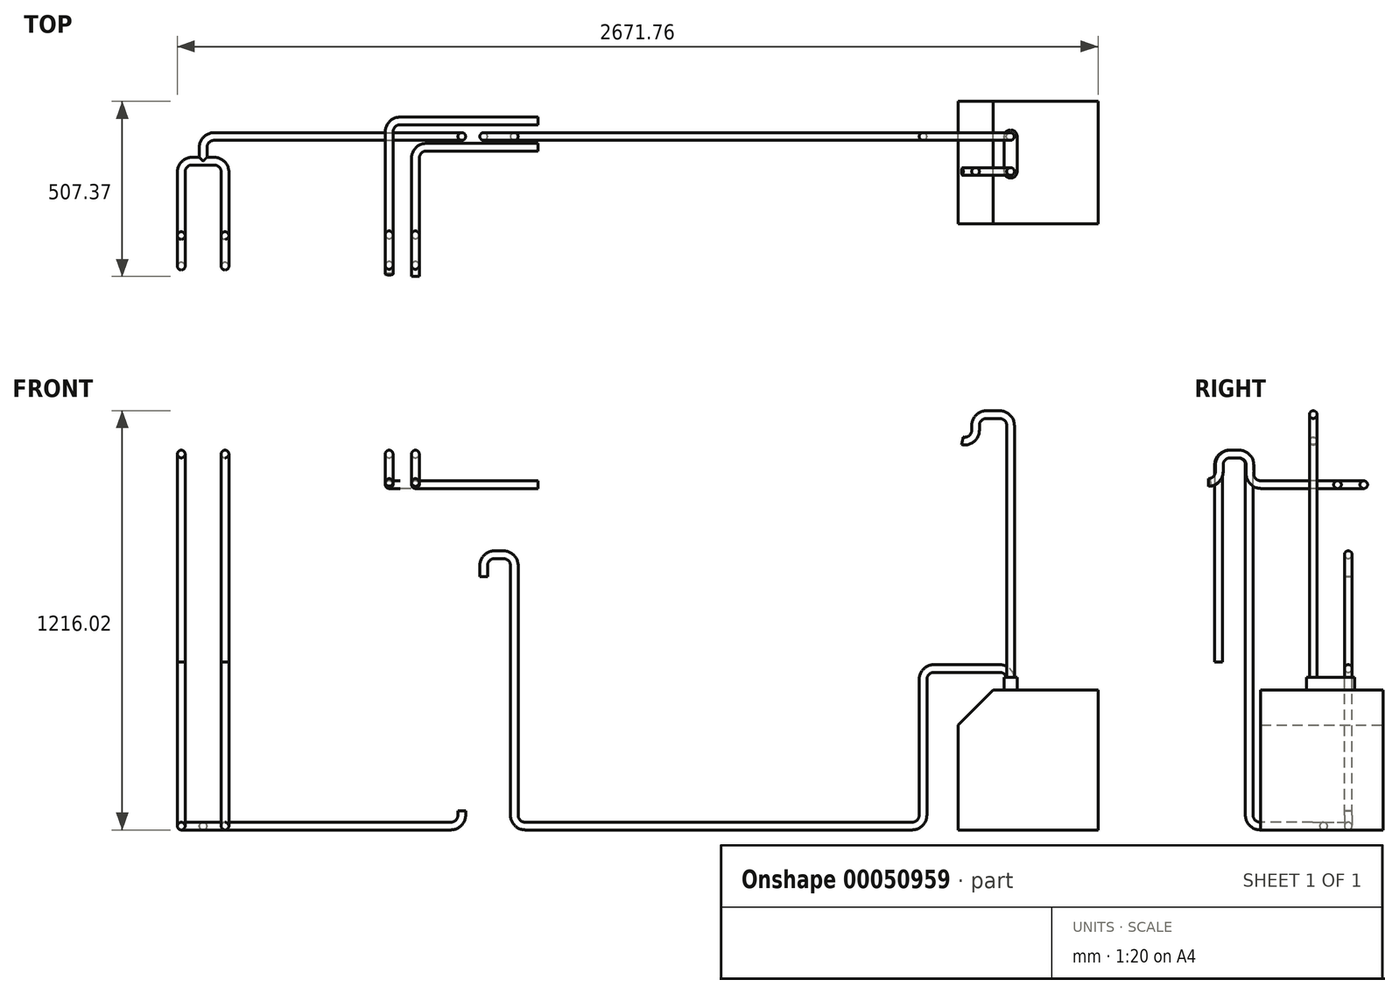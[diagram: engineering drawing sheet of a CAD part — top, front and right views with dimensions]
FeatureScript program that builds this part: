
annotation { "Feature Type Name" : "Feature", "Feature Type Description" : "" }
export const myFeature = defineFeature(function(context is Context, id is Id, definition is map)
    precondition{}
    {
        {
            var Q0;
            Q0=qCreatedBy(makeId("Right.planeOp"),FACE);
            var sketch = newSketch(context, id + "F0", { "sketchPlane" : qUnion([Q0])});
            skLineSegment(sketch, "E0", {"start": v(-273.05, 476.25) * mm, "end": v(-273.05, 1047.75) * mm});
            skLineSegment(sketch, "E1", {"start": v(-241.3, 1079.5) * mm, "end": v(-215.9, 1079.5) * mm});
            skLineSegment(sketch, "E2", {"start": v(-184.15, 1047.75) * mm, "end": v(-184.15, 31.75) * mm});
            skLineSegment(sketch, "E3", {"start": v(-152.4, 0) * mm, "end": v(0, 0) * mm});
            skPoint(sketch, "E4.visualSharp", {"position": v(-273.05, 1079.5) * mm});
            skArc(sketch, "E4.filletArc", {"start": v(-241.3, 1079.5) * mm, "mid": v(-263.75, 1070.2) * mm, "end": v(-273.05, 1047.75) * mm});
            skPoint(sketch, "E5.visualSharp", {"position": v(-184.15, 1079.5) * mm});
            skArc(sketch, "E5.filletArc", {"start": v(-184.15, 1047.75) * mm, "mid": v(-193.45, 1070.2) * mm, "end": v(-215.9, 1079.5) * mm});
            skPoint(sketch, "E6.visualSharp", {"position": v(-184.15, 0) * mm});
            skArc(sketch, "E6.filletArc", {"start": v(-184.15, 31.75) * mm, "mid": v(-174.85, 9.3) * mm, "end": v(-152.4, 0) * mm});
            skSolve(sketch);
        }
        {
            var Q0;
            Q0=qCreatedBy(makeId("Top.planeOp"),FACE);
            var sketch = newSketch(context, id + "F1", { "sketchPlane" : qUnion([Q0])});
            skLineSegment(sketch, "E7", {"start": v(31.75, 31.75) * mm, "end": v(95.25, 31.75) * mm});
            skPoint(sketch, "E8.visualSharp", {"position": v(-6.35, 31.75) * mm});
            skArc(sketch, "E8.filletArc", {"start": v(31.75, 31.75) * mm, "mid": v(9.3, 22.45) * mm, "end": v(0, 0) * mm});
            skPoint(sketch, "E9.visualSharp", {"position": v(280.99, 31.75) * mm});
            skArc(sketch, "E9.filletArc", {"start": v(127, 0) * mm, "mid": v(117.7, 22.45) * mm, "end": v(95.25, 31.75) * mm});
            skPoint(sketch, "E10.visualSharp", {"position": v(82.55, 82.55) * mm});
            skSolve(sketch);
        }
        {
            var Q0;
            Q0=qCreatedBy(makeId("Front.planeOp"),FACE);
            var sketch = newSketch(context, id + "F2", { "sketchPlane" : qUnion([Q0])});
            skCircle(sketch, "E11", {"center": v(0, 0) * mm, "radius": 11.11 * mm});
            skSolve(sketch);
        }
        {
            var Q0;
            Q0=qCreatedBy(makeId("Right.planeOp"),FACE);
            var Q1;
            Q1=sQuery(id+"F1.wireOp",VERTEX,"E9.filletArc.start");
            cPlane(context, id + "F3", {"entities" : qUnion([Q0, Q1]), "cplaneType" : CPlaneType.PLANE_POINT, "offset" : 25.4 * mm, "width" : 152.4 * mm, "height" : 152.4 * mm});
        }
        {
            var Q0;
            Q0=qCreatedBy(id+"F3.planeOp",FACE);
            var sketch = newSketch(context, id + "F4", { "sketchPlane" : qUnion([Q0])});
            skLineSegment(sketch, "E12", {"start": v(0, 0) * mm, "end": v(-152.4, 0) * mm});
            skLineSegment(sketch, "E13", {"start": v(-184.15, 31.75) * mm, "end": v(-184.15, 1047.75) * mm});
            skLineSegment(sketch, "E14", {"start": v(-215.9, 1079.5) * mm, "end": v(-241.3, 1079.5) * mm});
            skLineSegment(sketch, "E15", {"start": v(-273.05, 1047.75) * mm, "end": v(-273.05, 476.25) * mm});
            skPoint(sketch, "E16.visualSharp", {"position": v(-273.05, 1079.5) * mm});
            skArc(sketch, "E16.filletArc", {"start": v(-241.3, 1079.5) * mm, "mid": v(-263.75, 1070.2) * mm, "end": v(-273.05, 1047.75) * mm});
            skPoint(sketch, "E17.visualSharp", {"position": v(-184.15, 1079.5) * mm});
            skArc(sketch, "E17.filletArc", {"start": v(-184.15, 1047.75) * mm, "mid": v(-193.45, 1070.2) * mm, "end": v(-215.9, 1079.5) * mm});
            skPoint(sketch, "E18.visualSharp", {"position": v(-184.15, 0) * mm});
            skArc(sketch, "E18.filletArc", {"start": v(-184.15, 31.75) * mm, "mid": v(-174.85, 9.3) * mm, "end": v(-152.4, 0) * mm});
            skSolve(sketch);
        }
        {
            var Q0;
            Q0=makeQuery(id+"F2.imprint","IMPRINT",FACE,{"disambiguationData":[TD([[makeQuery(id+"F2.imprint","IMPRINT",EDGE,{"derivedFrom":sQuery(id+"F2.wireOp",EDGE,"E11")}),1.0]])]});
            var Q1;
            Q1 = qConstructionFilter(qBodyType(qCreatedBy(id + "F0" ,EDGE), BodyType.WIRE), ConstructionObject.NO);
            sweep(context, id + "F5", {"profiles" : qUnion([Q0]), "path" : qUnion([Q1])});
        }
        {
            var Q0;
            Q0=makeQuery(id+"F2.imprint","IMPRINT",FACE,{"disambiguationData":[TD([[makeQuery(id+"F2.imprint","IMPRINT",EDGE,{"derivedFrom":sQuery(id+"F2.wireOp",EDGE,"E11")}),1.0]])]});
            var Q1;
            Q1=sQuery(id+"F1.wireOp",EDGE,"E8.filletArc");
            var Q2;
            Q2=sQuery(id+"F1.wireOp",EDGE,"E7");
            var Q3;
            Q3=sQuery(id+"F1.wireOp",EDGE,"E9.filletArc");
            var Q4;
            Q4=sQuery(id+"F4.wireOp",EDGE,"E12");
            var Q5;
            Q5=sQuery(id+"F4.wireOp",EDGE,"E18.filletArc");
            var Q6;
            Q6=sQuery(id+"F4.wireOp",EDGE,"E13");
            var Q7;
            Q7=sQuery(id+"F4.wireOp",EDGE,"E17.filletArc");
            var Q8;
            Q8=sQuery(id+"F4.wireOp",EDGE,"E14");
            var Q9;
            Q9=sQuery(id+"F4.wireOp",EDGE,"E16.filletArc");
            var Q10;
            Q10=sQuery(id+"F4.wireOp",EDGE,"E15");
            sweep(context, id + "F6", {"operationType" : NewBodyOperationType.ADD, "profiles" : qUnion([Q0]), "path" : qUnion([Q1, Q2, Q3, Q4, Q5, Q6, Q7, Q8, Q9, Q10])});
        }
        {
            var Q0;
            Q0=qCreatedBy(makeId("Top.planeOp"),FACE);
            var sketch = newSketch(context, id + "F7", { "sketchPlane" : qUnion([Q0])});
            skLineSegment(sketch, "E19", {"start": v(63.5, 31.75) * mm, "end": v(63.5, 71.48) * mm});
            skLineSegment(sketch, "E20", {"start": v(95.25, 103.23) * mm, "end": v(782.32, 103.23) * mm});
            skPoint(sketch, "E21.visualSharp", {"position": v(63.5, 103.23) * mm});
            skArc(sketch, "E21.filletArc", {"start": v(95.25, 103.23) * mm, "mid": v(72.8, 93.93) * mm, "end": v(63.5, 71.48) * mm});
            skLineSegment(sketch, "E22.trimOffspring", {"start": v(998.22, 103.23) * mm, "end": v(2120.9, 103.23) * mm});
            skSolve(sketch);
        }
        {
            var Q0;
            Q0=qCreatedBy(makeId("Right.planeOp"),FACE);
            var Q1;
            Q1=sQuery(id+"F7.wireOp",VERTEX,"E22.trimOffspring.start");
            cPlane(context, id + "F8", {"entities" : qUnion([Q0, Q1]), "cplaneType" : CPlaneType.PLANE_POINT, "offset" : 25.4 * mm, "width" : 152.4 * mm, "height" : 152.4 * mm});
        }
        {
            var Q0;
            Q0=qCreatedBy(id+"F8.planeOp",FACE);
            var sketch = newSketch(context, id + "F9", { "sketchPlane" : qUnion([Q0])});
            skCircle(sketch, "E23", {"center": v(103.23, 0) * mm, "radius": 11.11 * mm});
            skSolve(sketch);
        }
        {
            var Q0;
            Q0=makeQuery(id+"F9.imprint","IMPRINT",FACE,{"disambiguationData":[TD([[makeQuery(id+"F9.imprint","IMPRINT",EDGE,{"derivedFrom":sQuery(id+"F9.wireOp",EDGE,"E23")}),1.0]])]});
            var Q1;
            Q1=sQuery(id+"F7.wireOp",EDGE,"E22.trimOffspring");
            sweep(context, id + "F10", {"profiles" : qUnion([Q0]), "path" : qUnion([Q1])});
        }
        {
            var Q0;
            Q0=sQuery(id+"F1.wireOp",EDGE,"E7");
            cPoint(context, id + "F11", {"entities" : qUnion([Q0]), "parameter" : 0.5});
        }
        {
            var Q0;
            Q0=qCreatedBy(makeId("Front.planeOp"),FACE);
            var Q1;
            Q1 = qCreatedBy(id + "F11" ,VERTEX);
            cPlane(context, id + "F12", {"entities" : qUnion([Q0, Q1]), "cplaneType" : CPlaneType.PLANE_POINT, "offset" : 25.4 * mm, "width" : 152.4 * mm, "height" : 152.4 * mm});
        }
        {
            var Q0;
            Q0=qCreatedBy(id+"F12.planeOp",FACE);
            var sketch = newSketch(context, id + "F13", { "sketchPlane" : qUnion([Q0])});
            skCircle(sketch, "E24", {"center": v(63.5, 0) * mm, "radius": 11.11 * mm});
            skSolve(sketch);
        }
        {
            var Q0;
            Q0=qCreatedBy(makeId("Front.planeOp"),FACE);
            var Q1;
            Q1=sQuery(id+"F7.wireOp",VERTEX,"E20.end");
            cPlane(context, id + "F14", {"entities" : qUnion([Q0, Q1]), "cplaneType" : CPlaneType.PLANE_POINT, "offset" : 25.4 * mm, "width" : 152.4 * mm, "height" : 152.4 * mm});
        }
        {
            var Q0;
            Q0 = qSketchRegion(id + "F13", true);
            var Q1;
            Q1=sQuery(id+"F7.wireOp",EDGE,"E19");
            var Q2;
            Q2=sQuery(id+"F7.wireOp",EDGE,"E21.filletArc");
            var Q3;
            Q3=sQuery(id+"F7.wireOp",EDGE,"E20");
            sweep(context, id + "F15", {"operationType" : NewBodyOperationType.ADD, "profiles" : qUnion([Q0]), "path" : qUnion([Q1, Q2, Q3])});
        }
        {
            var Q0;
            Q0=qCreatedBy(id+"F14.planeOp",FACE);
            var sketch = newSketch(context, id + "F16", { "sketchPlane" : qUnion([Q0])});
            skLineSegment(sketch, "E25", {"start": v(2152.65, 31.75) * mm, "end": v(2152.65, 425.45) * mm});
            skLineSegment(sketch, "E26", {"start": v(2184.4, 457.2) * mm, "end": v(2374.9, 457.2) * mm});
            skLineSegment(sketch, "E27", {"start": v(2406.65, 425.45) * mm, "end": v(2406.65, 395.29) * mm});
            skPoint(sketch, "E28.visualSharp", {"position": v(2152.65, 0) * mm});
            skArc(sketch, "E28.filletArc", {"start": v(2120.9, 0) * mm, "mid": v(2143.35, 9.3) * mm, "end": v(2152.65, 31.75) * mm});
            skPoint(sketch, "E29.visualSharp", {"position": v(2152.65, 457.2) * mm});
            skArc(sketch, "E29.filletArc", {"start": v(2184.4, 457.2) * mm, "mid": v(2161.95, 447.9) * mm, "end": v(2152.65, 425.45) * mm});
            skPoint(sketch, "E30.visualSharp", {"position": v(2406.65, 457.2) * mm});
            skArc(sketch, "E30.filletArc", {"start": v(2406.65, 425.45) * mm, "mid": v(2397.35, 447.9) * mm, "end": v(2374.9, 457.2) * mm});
            skLineSegment(sketch, "E31.bottom", {"start": v(2355.85, 395.29) * mm, "end": v(2660.65, 395.29) * mm});
            skLineSegment(sketch, "E31.top", {"start": v(2254.25, -11.11) * mm, "end": v(2660.65, -11.11) * mm});
            skLineSegment(sketch, "E31.left", {"start": v(2254.25, 293.69) * mm, "end": v(2254.25, -11.11) * mm});
            skLineSegment(sketch, "E31.right", {"start": v(2660.65, 395.29) * mm, "end": v(2660.65, -11.11) * mm});
            skLineSegment(sketch, "E32", {"start": v(2254.25, 293.69) * mm, "end": v(2355.85, 395.29) * mm});
            skSolve(sketch);
        }
        {
            var Q0;
            Q0 = qSketchRegion(id + "F16", true);
            extrude(context, id + "F17", {"entities" : qUnion([Q0]), "depth" : 254 * mm, "hasSecondDirection" : true, "secondDirectionOppositeDirection" : true, "secondDirectionDepth" : 101.6 * mm});
        }
        {
            var Q0;
            Q0=makeQuery(id+"F10.opSweep","CAP_FACE",FACE,{"disambiguationData":[OSD([sQuery(id+"F7.wireOp",VERTEX,"E22.trimOffspring.end"),sQuery(id+"F9.wireOp",EDGE,"E23")])],"isStart":false});
            var Q1;
            Q1=sQuery(id+"F16.wireOp",EDGE,"Az77wKnU-HWYb-h9Rr-81SB-TqBPY5BJPOyP");
            var Q2;
            Q2=sQuery(id+"F16.wireOp",EDGE,"E28.filletArc");
            var Q3;
            Q3=sQuery(id+"F16.wireOp",EDGE,"E25");
            var Q4;
            Q4=sQuery(id+"F16.wireOp",EDGE,"E29.filletArc");
            var Q5;
            Q5=sQuery(id+"F16.wireOp",EDGE,"E26");
            var Q6;
            Q6=sQuery(id+"F16.wireOp",EDGE,"E30.filletArc");
            var Q7;
            Q7=sQuery(id+"F16.wireOp",EDGE,"E27");
            sweep(context, id + "F18", {"operationType" : NewBodyOperationType.ADD, "profiles" : qUnion([Q0]), "path" : qUnion([Q1, Q2, Q3, Q4, Q5, Q6, Q7])});
        }
        {
            var Q0;
            Q0=qCreatedBy(id+"F14.planeOp",FACE);
            cPlane(context, id + "F19", {"entities" : qUnion([Q0]), "cplaneType" : CPlaneType.OFFSET, "offset" : 101.6 * mm, "width" : 152.4 * mm, "height" : 152.4 * mm});
        }
        {
            var Q0;
            Q0=qCreatedBy(id+"F19.planeOp",FACE);
            var sketch = newSketch(context, id + "F20", { "sketchPlane" : qUnion([Q0])});
            skLineSegment(sketch, "E33", {"start": v(2406.65, 381) * mm, "end": v(2406.65, 1162.05) * mm});
            skLineSegment(sketch, "E34", {"start": v(2305.05, 1162.05) * mm, "end": v(2305.05, 1148.7) * mm});
            skLineSegment(sketch, "E35", {"start": v(2336.8, 1193.8) * mm, "end": v(2374.9, 1193.8) * mm});
            skPoint(sketch, "E36.visualSharp", {"position": v(2406.65, 1193.8) * mm});
            skArc(sketch, "E36.filletArc", {"start": v(2406.65, 1162.05) * mm, "mid": v(2397.35, 1184.5) * mm, "end": v(2374.9, 1193.8) * mm});
            skPoint(sketch, "E37.visualSharp", {"position": v(2305.05, 1193.8) * mm});
            skArc(sketch, "E37.filletArc", {"start": v(2336.8, 1193.8) * mm, "mid": v(2314.35, 1184.5) * mm, "end": v(2305.05, 1162.05) * mm});
            skPoint(sketch, "E38.visualSharp", {"position": v(2305.05, 1092.2) * mm});
            skArc(sketch, "E38.filletArc", {"start": v(2266.95, 1117.6) * mm, "mid": v(2293.38, 1124.12) * mm, "end": v(2305.05, 1148.7) * mm});
            skSolve(sketch);
        }
        {
            var Q0;
            Q0=qCreatedBy(makeId("Top.planeOp"),FACE);
            var Q1;
            Q1=sQuery(id+"F20.wireOp",VERTEX,"E33.start");
            cPlane(context, id + "F21", {"entities" : qUnion([Q0, Q1]), "cplaneType" : CPlaneType.PLANE_POINT, "offset" : 25.4 * mm, "width" : 152.4 * mm, "height" : 152.4 * mm});
        }
        {
            var Q0;
            Q0=qCreatedBy(id+"F21.planeOp",FACE);
            var sketch = newSketch(context, id + "F22", { "sketchPlane" : qUnion([Q0])});
            skCircle(sketch, "E39", {"center": v(2406.65, 1.63) * mm, "radius": 11.11 * mm});
            skArc(sketch, "E40", {"start": v(2387.6, 1.63) * mm, "mid": v(2406.65, -17.42) * mm, "end": v(2425.7, 1.63) * mm});
            skLineSegment(sketch, "E41", {"start": v(2387.6, 1.63) * mm, "end": v(2387.6, 103.23) * mm});
            skLineSegment(sketch, "E42", {"start": v(2425.7, 1.63) * mm, "end": v(2425.7, 103.23) * mm});
            skArc(sketch, "E43", {"start": v(2425.7, 103.23) * mm, "mid": v(2406.65, 122.28) * mm, "end": v(2387.6, 103.23) * mm});
            skSolve(sketch);
        }
        {
            var Q0;
            Q0=makeQuery(id+"F22.imprint","IMPRINT",FACE,{"disambiguationData":[TD([[makeQuery(id+"F22.imprint","IMPRINT",EDGE,{"derivedFrom":sQuery(id+"F22.wireOp",EDGE,"E39")}),1.0]])]});
            var Q1;
            Q1=sQuery(id+"F20.wireOp",EDGE,"E33");
            var Q2;
            Q2=sQuery(id+"F20.wireOp",EDGE,"E36.filletArc");
            var Q3;
            Q3=sQuery(id+"F20.wireOp",EDGE,"E35");
            var Q4;
            Q4=sQuery(id+"F20.wireOp",EDGE,"E37.filletArc");
            var Q5;
            Q5=sQuery(id+"F20.wireOp",EDGE,"E34");
            var Q6;
            Q6=sQuery(id+"F20.wireOp",EDGE,"E38.filletArc");
            sweep(context, id + "F23", {"profiles" : qUnion([Q0]), "path" : qUnion([Q1, Q2, Q3, Q4, Q5, Q6])});
        }
        {
            var Q0;
            Q0 = qSketchRegion(id + "F22", true);
            extrude(context, id + "F24", {"entities" : qUnion([Q0]), "operationType" : NewBodyOperationType.ADD, "depth" : 50.8 * mm});
        }
        {
            var Q0;
            Q0=qCreatedBy(makeId("Top.planeOp"),FACE);
            cPlane(context, id + "F25", {"entities" : qUnion([Q0]), "cplaneType" : CPlaneType.OFFSET, "offset" : 990.6 * mm, "width" : 152.4 * mm, "height" : 152.4 * mm});
        }
        {
            var Q0;
            Q0=qCreatedBy(id+"F25.planeOp",FACE);
            var sketch = newSketch(context, id + "F26", { "sketchPlane" : qUnion([Q0])});
            skLineSegment(sketch, "E44", {"start": v(603.25, 116.56) * mm, "end": v(603.25, -150.14) * mm});
            skLineSegment(sketch, "E45", {"start": v(635, 148.31) * mm, "end": v(1035.05, 148.31) * mm});
            skPoint(sketch, "E46.visualSharp", {"position": v(603.25, 148.31) * mm});
            skArc(sketch, "E46.filletArc", {"start": v(635, 148.31) * mm, "mid": v(612.55, 139.01) * mm, "end": v(603.25, 116.56) * mm});
            skLineSegment(sketch, "E47", {"start": v(1035.05, 72.11) * mm, "end": v(711.2, 72.11) * mm});
            skLineSegment(sketch, "E48", {"start": v(679.45, 40.36) * mm, "end": v(679.45, -150.14) * mm});
            skPoint(sketch, "E49.visualSharp", {"position": v(679.45, 72.11) * mm});
            skArc(sketch, "E49.filletArc", {"start": v(711.2, 72.11) * mm, "mid": v(688.75, 62.81) * mm, "end": v(679.45, 40.36) * mm});
            skSolve(sketch);
        }
        {
            var Q0;
            Q0=qCreatedBy(makeId("Right.planeOp"),FACE);
            var Q1;
            Q1=sQuery(id+"F26.wireOp",VERTEX,"E45.end");
            cPlane(context, id + "F27", {"entities" : qUnion([Q0, Q1]), "cplaneType" : CPlaneType.PLANE_POINT, "offset" : 25.4 * mm, "width" : 152.4 * mm, "height" : 152.4 * mm});
        }
        {
            var Q0;
            Q0=qCreatedBy(id+"F27.planeOp",FACE);
            var sketch = newSketch(context, id + "F28", { "sketchPlane" : qUnion([Q0])});
            skCircle(sketch, "E50", {"center": v(148.31, 990.6) * mm, "radius": 11.11 * mm});
            skCircle(sketch, "E51", {"center": v(72.11, 990.6) * mm, "radius": 11.11 * mm});
            skSolve(sketch);
        }
        {
            var Q0;
            Q0=qCreatedBy(id+"F27.planeOp",FACE);
            var Q1;
            Q1=sQuery(id+"F26.wireOp",VERTEX,"E44.end");
            cPlane(context, id + "F29", {"entities" : qUnion([Q0, Q1]), "cplaneType" : CPlaneType.PLANE_POINT, "offset" : 25.4 * mm, "width" : 152.4 * mm, "height" : 152.4 * mm});
        }
        {
            var Q0;
            Q0=qCreatedBy(id+"F29.planeOp",FACE);
            var sketch = newSketch(context, id + "F30", { "sketchPlane" : qUnion([Q0])});
            skLineSegment(sketch, "E52", {"start": v(-181.89, 1022.35) * mm, "end": v(-181.89, 1047.75) * mm});
            skLineSegment(sketch, "E53", {"start": v(-213.64, 1079.5) * mm, "end": v(-239.04, 1079.5) * mm});
            skLineSegment(sketch, "E54", {"start": v(-270.79, 1047.75) * mm, "end": v(-270.79, 1028.06) * mm});
            skPoint(sketch, "E55.visualSharp", {"position": v(-270.79, 1123.55) * mm});
            skArc(sketch, "E55.filletArc", {"start": v(-296.19, 996.95) * mm, "mid": v(-277.94, 1007.98) * mm, "end": v(-270.79, 1028.06) * mm});
            skPoint(sketch, "E56.visualSharp", {"position": v(-270.79, 1079.5) * mm});
            skArc(sketch, "E56.filletArc", {"start": v(-239.04, 1079.5) * mm, "mid": v(-261.49, 1070.2) * mm, "end": v(-270.79, 1047.75) * mm});
            skPoint(sketch, "E57.visualSharp", {"position": v(-181.89, 1079.5) * mm});
            skArc(sketch, "E57.filletArc", {"start": v(-181.89, 1047.75) * mm, "mid": v(-191.19, 1070.2) * mm, "end": v(-213.64, 1079.5) * mm});
            skPoint(sketch, "E58.visualSharp", {"position": v(-181.89, 1009.84) * mm});
            skArc(sketch, "E58.filletArc", {"start": v(-181.89, 1022.35) * mm, "mid": v(-172.59, 999.9) * mm, "end": v(-150.14, 990.6) * mm});
            skSolve(sketch);
        }
        {
            var Q0;
            Q0=makeQuery(id+"F28.imprint","IMPRINT",FACE,{"disambiguationData":[TD([[makeQuery(id+"F28.imprint","IMPRINT",EDGE,{"derivedFrom":sQuery(id+"F28.wireOp",EDGE,"E50")}),1.0]])]});
            var Q1;
            Q1=sQuery(id+"F26.wireOp",EDGE,"E45");
            var Q2;
            Q2=sQuery(id+"F26.wireOp",EDGE,"E46.filletArc");
            var Q3;
            Q3=sQuery(id+"F26.wireOp",EDGE,"E44");
            var Q4;
            Q4=sQuery(id+"F30.wireOp",EDGE,"E58.filletArc");
            var Q5;
            Q5=sQuery(id+"F30.wireOp",EDGE,"E52");
            var Q6;
            Q6=sQuery(id+"F30.wireOp",EDGE,"E57.filletArc");
            var Q7;
            Q7=sQuery(id+"F30.wireOp",EDGE,"E53");
            var Q8;
            Q8=sQuery(id+"F30.wireOp",EDGE,"E56.filletArc");
            var Q9;
            Q9=sQuery(id+"F30.wireOp",EDGE,"E54");
            var Q10;
            Q10=sQuery(id+"F30.wireOp",EDGE,"E55.filletArc");
            sweep(context, id + "F31", {"profiles" : qUnion([Q0]), "path" : qUnion([Q1, Q2, Q3, Q4, Q5, Q6, Q7, Q8, Q9, Q10])});
        }
        {
            var Q0;
            Q0=qCreatedBy(id+"F29.planeOp",FACE);
            var Q1;
            Q1=sQuery(id+"F26.wireOp",VERTEX,"E48.end");
            cPlane(context, id + "F32", {"entities" : qUnion([Q0, Q1]), "cplaneType" : CPlaneType.PLANE_POINT, "offset" : 25.4 * mm, "width" : 152.4 * mm, "height" : 152.4 * mm});
        }
        {
            var Q0;
            Q0=qCreatedBy(id+"F32.planeOp",FACE);
            var sketch = newSketch(context, id + "F33", { "sketchPlane" : qUnion([Q0])});
            skLineSegment(sketch, "E59", {"start": v(-181.89, 1022.35) * mm, "end": v(-181.89, 1047.75) * mm});
            skLineSegment(sketch, "E60", {"start": v(-213.64, 1079.5) * mm, "end": v(-239.04, 1079.5) * mm});
            skLineSegment(sketch, "E61", {"start": v(-270.79, 1047.75) * mm, "end": v(-270.79, 1028.7) * mm});
            skPoint(sketch, "E62.visualSharp", {"position": v(-270.79, 1021) * mm});
            skArc(sketch, "E62.filletArc", {"start": v(-302.54, 996.95) * mm, "mid": v(-280.09, 1006.25) * mm, "end": v(-270.79, 1028.7) * mm});
            skPoint(sketch, "E63.visualSharp", {"position": v(-270.79, 1079.5) * mm});
            skArc(sketch, "E63.filletArc", {"start": v(-239.04, 1079.5) * mm, "mid": v(-261.49, 1070.2) * mm, "end": v(-270.79, 1047.75) * mm});
            skPoint(sketch, "E64.visualSharp", {"position": v(-181.89, 1079.5) * mm});
            skArc(sketch, "E64.filletArc", {"start": v(-181.89, 1047.75) * mm, "mid": v(-191.19, 1070.2) * mm, "end": v(-213.64, 1079.5) * mm});
            skPoint(sketch, "E65.visualSharp", {"position": v(-181.89, 992.4) * mm});
            skArc(sketch, "E65.filletArc", {"start": v(-181.89, 1022.35) * mm, "mid": v(-172.59, 999.9) * mm, "end": v(-150.14, 990.6) * mm});
            skSolve(sketch);
        }
        {
            var Q0;
            Q0=makeQuery(id+"F28.imprint","IMPRINT",FACE,{"disambiguationData":[TD([[makeQuery(id+"F28.imprint","IMPRINT",EDGE,{"derivedFrom":sQuery(id+"F28.wireOp",EDGE,"E51")}),1.0]])]});
            var Q1;
            Q1=sQuery(id+"F26.wireOp",EDGE,"E47");
            var Q2;
            Q2=sQuery(id+"F26.wireOp",EDGE,"E49.filletArc");
            var Q3;
            Q3=sQuery(id+"F26.wireOp",EDGE,"E48");
            var Q4;
            Q4=sQuery(id+"F33.wireOp",EDGE,"E65.filletArc");
            var Q5;
            Q5=sQuery(id+"F33.wireOp",EDGE,"E59");
            var Q6;
            Q6=sQuery(id+"F33.wireOp",EDGE,"E64.filletArc");
            var Q7;
            Q7=sQuery(id+"F33.wireOp",EDGE,"E60");
            var Q8;
            Q8=sQuery(id+"F33.wireOp",EDGE,"E63.filletArc");
            var Q9;
            Q9=sQuery(id+"F33.wireOp",EDGE,"E61");
            var Q10;
            Q10=sQuery(id+"F33.wireOp",EDGE,"E62.filletArc");
            sweep(context, id + "F34", {"profiles" : qUnion([Q0]), "path" : qUnion([Q1, Q2, Q3, Q4, Q5, Q6, Q7, Q8, Q9, Q10])});
        }
        {
            var Q0;
            Q0=qCreatedBy(id+"F14.planeOp",FACE);
            var sketch = newSketch(context, id + "F35", { "sketchPlane" : qUnion([Q0])});
            skLineSegment(sketch, "E66", {"start": v(814.07, 31.75) * mm, "end": v(814.07, 44.45) * mm});
            skPoint(sketch, "E67.visualSharp", {"position": v(814.07, 0) * mm});
            skArc(sketch, "E67.filletArc", {"start": v(782.32, 0) * mm, "mid": v(804.77, 9.3) * mm, "end": v(814.07, 31.75) * mm});
            skLineSegment(sketch, "E68", {"start": v(966.47, 31.75) * mm, "end": v(966.47, 755.65) * mm});
            skLineSegment(sketch, "E69", {"start": v(934.72, 787.4) * mm, "end": v(909.32, 787.4) * mm});
            skLineSegment(sketch, "E70", {"start": v(877.57, 755.65) * mm, "end": v(877.57, 724.29) * mm});
            skPoint(sketch, "E71.visualSharp", {"position": v(966.47, -19.72) * mm});
            skArc(sketch, "E71.filletArc", {"start": v(966.47, 31.75) * mm, "mid": v(975.76, 9.3) * mm, "end": v(998.22, 0) * mm});
            skPoint(sketch, "E72.visualSharp", {"position": v(966.47, 787.4) * mm});
            skArc(sketch, "E72.filletArc", {"start": v(966.47, 755.65) * mm, "mid": v(957.17, 778.1) * mm, "end": v(934.72, 787.4) * mm});
            skPoint(sketch, "E73.visualSharp", {"position": v(877.57, 787.4) * mm});
            skArc(sketch, "E73.filletArc", {"start": v(909.32, 787.4) * mm, "mid": v(886.86, 778.1) * mm, "end": v(877.57, 755.65) * mm});
            skSolve(sketch);
        }
        {
            var Q0;
            Q0=makeQuery(id+"F15.opSweep","CAP_FACE",FACE,{"disambiguationData":[OSD([sQuery(id+"F7.wireOp",VERTEX,"E20.end"),sQuery(id+"F13.wireOp",EDGE,"E24")])],"isStart":false});
            var Q1;
            Q1=sQuery(id+"F35.wireOp",EDGE,"E67.filletArc");
            var Q2;
            Q2=sQuery(id+"F35.wireOp",EDGE,"E66");
            sweep(context, id + "F36", {"operationType" : NewBodyOperationType.ADD, "profiles" : qUnion([Q0]), "path" : qUnion([Q1, Q2])});
        }
        {
            var Q0;
            Q0=makeQuery(id+"F10.opSweep","CAP_FACE",FACE,{"disambiguationData":[OSD([sQuery(id+"F7.wireOp",VERTEX,"E22.trimOffspring.start"),sQuery(id+"F9.wireOp",EDGE,"E23")])],"isStart":true});
            var Q1;
            Q1=sQuery(id+"F35.wireOp",EDGE,"E71.filletArc");
            var Q2;
            Q2=sQuery(id+"F35.wireOp",EDGE,"E68");
            var Q3;
            Q3=sQuery(id+"F35.wireOp",EDGE,"E72.filletArc");
            var Q4;
            Q4=sQuery(id+"F35.wireOp",EDGE,"E69");
            var Q5;
            Q5=sQuery(id+"F35.wireOp",EDGE,"E73.filletArc");
            var Q6;
            Q6=sQuery(id+"F35.wireOp",EDGE,"E70");
            sweep(context, id + "F37", {"operationType" : NewBodyOperationType.ADD, "profiles" : qUnion([Q0]), "path" : qUnion([Q1, Q2, Q3, Q4, Q5, Q6])});
        }
    });
